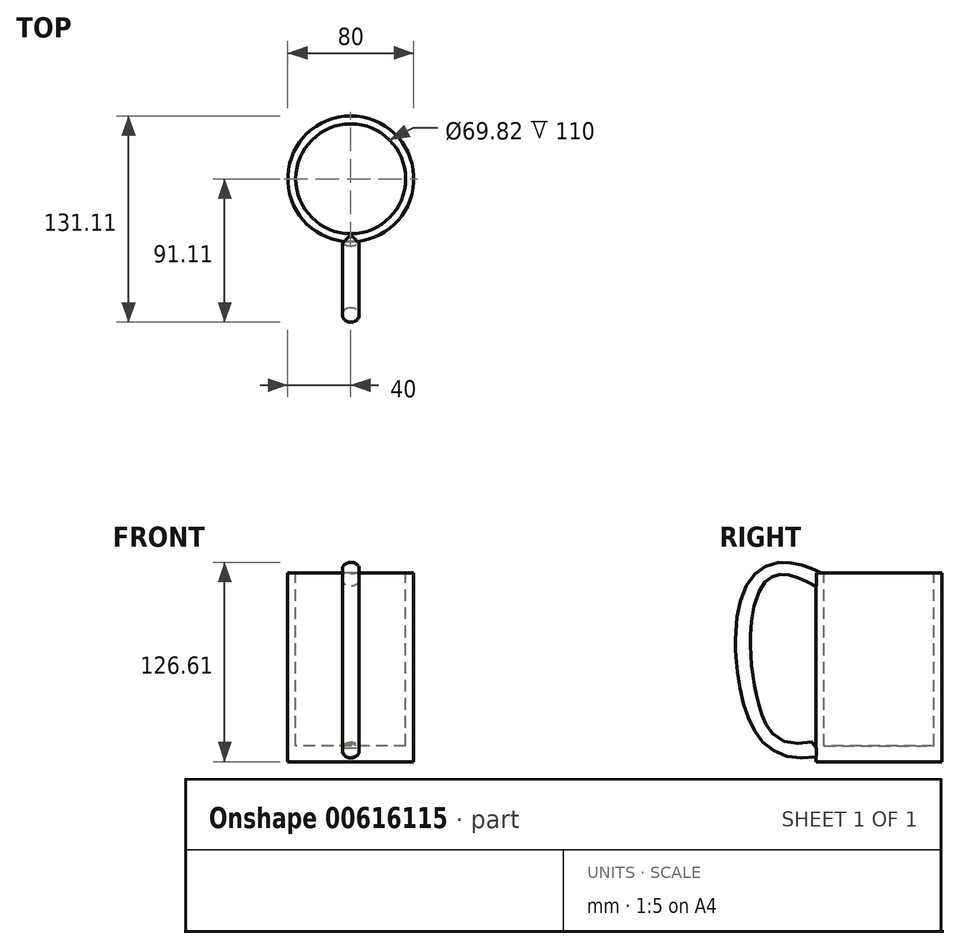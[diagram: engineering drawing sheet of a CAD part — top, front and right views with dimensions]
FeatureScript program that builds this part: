
annotation { "Feature Type Name" : "Feature", "Feature Type Description" : "" }
export const myFeature = defineFeature(function(context is Context, id is Id, definition is map)
    precondition{}
    {
        {
            var Q0;
            Q0=qCreatedBy(makeId("Top.planeOp"),FACE);
            var sketch = newSketch(context, id + "F0", { "sketchPlane" : qUnion([Q0])});
            skCircle(sketch, "E0", {"center": v(0, 0) * mm, "radius": 40 * mm});
            skSolve(sketch);
        }
        {
            var Q0;
            Q0=makeQuery(id+"F0.imprint","IMPRINT",FACE,{"disambiguationData":[TD([[makeQuery(id+"F0.imprint","IMPRINT",EDGE,{"derivedFrom":sQuery(id+"F0.wireOp",EDGE,"E0")}),1.0]])]});
            extrude(context, id + "F1", {"entities" : qUnion([Q0]), "depth" : 120 * mm, "offsetDistance" : 25 * mm});
        }
        {
            var Q0;
            Q0=qCreatedBy(makeId("Front.planeOp"),FACE);
            cPlane(context, id + "F2", {"entities" : qUnion([Q0]), "cplaneType" : CPlaneType.OFFSET, "offset" : 25 * mm, "width" : 150 * mm, "height" : 150 * mm});
        }
        {
            var Q0;
            Q0=qCreatedBy(makeId("Right.planeOp"),FACE);
            var sketch = newSketch(context, id + "F3", { "sketchPlane" : qUnion([Q0])});
            skFitSpline(sketch, "E1", {"points": [v(-35.5, 104.36) * mm, v(-70.32, 107.81) * mm, v(-65.5, 24.4) * mm, v(-33.78, 18.19) * mm], "startDerivative": vector(-143.9, 66.85) * mm, "endDerivative": vector(129.32, 25.53) * mm});
            skSolve(sketch);
        }
        {
            var Q0;
            Q0=qCreatedBy(id+"F2.planeOp",FACE);
            var sketch = newSketch(context, id + "F4", { "sketchPlane" : qUnion([Q0])});
            skCircle(sketch, "E2", {"center": v(0, 109.19) * mm, "radius": 5.36 * mm});
            skSolve(sketch);
        }
        {
            var Q0;
            Q0=makeQuery(id+"F4.imprint","IMPRINT",FACE,{"disambiguationData":[TD([[makeQuery(id+"F4.imprint","IMPRINT",EDGE,{"derivedFrom":sQuery(id+"F4.wireOp",EDGE,"E2")}),1.0]])]});
            var Q1;
            Q1=sQuery(id+"F3.wireOp",EDGE,"E1");
            sweep(context, id + "F5", {"operationType" : NewBodyOperationType.ADD, "profiles" : qUnion([Q0]), "path" : qUnion([Q1])});
        }
        {
            var Q0;
            Q0=makeQuery(id+"F1.opExtrude","CAP_FACE",FACE,{"disambiguationData":[OSD([sQuery(id+"F0.wireOp",EDGE,"E0")])],"isStart":false});
            var sketch = newSketch(context, id + "F6", { "sketchPlane" : qUnion([Q0])});
            skCircle(sketch, "E3", {"center": v(0, 0) * mm, "radius": 34.91 * mm});
            skSolve(sketch);
        }
        {
            var Q0;
            Q0=makeQuery(id+"F6.imprint","IMPRINT",FACE,{"disambiguationData":[TD([[makeQuery(id+"F6.imprint","IMPRINT",EDGE,{"derivedFrom":sQuery(id+"F6.wireOp",EDGE,"E3")}),1.0]])]});
            var Q1;
            Q1=sQuery(id+"F6.wireOp",EDGE,"E3");
            extrude(context, id + "F7", {"entities" : qUnion([Q0]), "operationType" : NewBodyOperationType.REMOVE, "surfaceEntities" : qUnion([Q1]), "oppositeDirection" : true, "depth" : 110 * mm, "offsetDistance" : 25 * mm});
        }
    });
